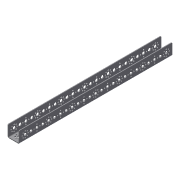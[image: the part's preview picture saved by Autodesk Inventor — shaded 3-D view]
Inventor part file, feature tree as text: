
AUTODESK INVENTOR PART (.ipt)
format: ipt  version: 2013 (Build 170138000, 138)  size: 557,568 bytes
history: native  units: in
note: dims shown in document units (in); Inventor stores cm internally (conversion verified against a paired STEP export)
features: hole x28, other x5, sketch x3
ambient origin geometry x8: Origin, YZ Plane, XZ Plane, XY Plane, X Axis, Y Axis, Z Axis, Center Point
bodies: Solid1 (feature_tree)
feature tree (36):
  other  "Tetrix Channel 416mm.ipt"
  other  "Blocks"
  hole  "Hole Pattern 4"  [1 undecoded]
  hole  "Hole Pattern 8"  [1 undecoded]
  other  "416 mm hole pattern"
  other  "Solid1::Tetrix Channel 416mm.ipt"
  other  "TaggingFeature1"
  sketch  "Sketch1"  dims[d0=0.3937in]
  sketch  "Sketch2"  dims[d1=16.378in d3=0.6299in d4=0.1457in d6=0.6299in d8=0.6299in d9=0.6299in d10=0.315in d13=0.1457in d14=0.315in d15=3.1496in d20=0.6299in d21=0.6299in d22=0.6299in d23=0.6299in d25=0.6299in d26=0.6299in d27=0.0787in d28=0.0787in d29=0.0394in d30=0.1575in d31=0.0787in d32=1.2598in d33=90.0deg d34=0.0787in d35=0.315in d36=0.0787in d37=0.0787in d38=0.6299in d39=0.6299in d40=0.6299in d41=0.6299in d42=0.6299in d43=0.6299in d45=0.6299in d47=0.0in d48=0.0787in d17=360.0deg]
  sketch  "Sketch3"
  hole  "Hole Pattern 4:1"  [1 undecoded]
  hole  "Hole Pattern 8:1"  [1 undecoded]
  hole  "Hole Pattern 8:2"  [1 undecoded]
  hole  "Hole Pattern 4:2"  [1 undecoded]
  hole  "Hole Pattern 8:3"  [1 undecoded]
  hole  "Hole Pattern 4:3"  [1 undecoded]
  hole  "Hole Pattern 8:4"  [1 undecoded]
  hole  "Hole Pattern 4:4"  [1 undecoded]
  hole  "Hole Pattern 8:5"  [1 undecoded]
  hole  "Hole Pattern 8:6"  [1 undecoded]
  hole  "Hole Pattern 4:5"  [1 undecoded]
  hole  "Hole Pattern 8:7"  [1 undecoded]
  hole  "Hole Pattern 4:6"  [1 undecoded]
  hole  "Hole Pattern 4:1_1"  [1 undecoded]
  hole  "Hole Pattern 8:1_1"  [1 undecoded]
  hole  "Hole Pattern 8:2_1"  [1 undecoded]
  hole  "Hole Pattern 4:2_1"  [1 undecoded]
  hole  "Hole Pattern 8:3_1"  [1 undecoded]
  hole  "Hole Pattern 4:3_1"  [1 undecoded]
  hole  "Hole Pattern 8:4_1"  [1 undecoded]
  hole  "Hole Pattern 4:4_1"  [1 undecoded]
  hole  "Hole Pattern 8:5_1"  [1 undecoded]
  hole  "Hole Pattern 8:6_1"  [1 undecoded]
  hole  "Hole Pattern 4:5_1"  [1 undecoded]
  hole  "Hole Pattern 8:7_1"  [1 undecoded]
  hole  "Hole Pattern 4:6_1"  [1 undecoded]
note: 28 required parameter values undecoded (feature->parameter linkage not recoverable at this tier; creation-order binding heuristic only, values carry confidence <= 0.55)
